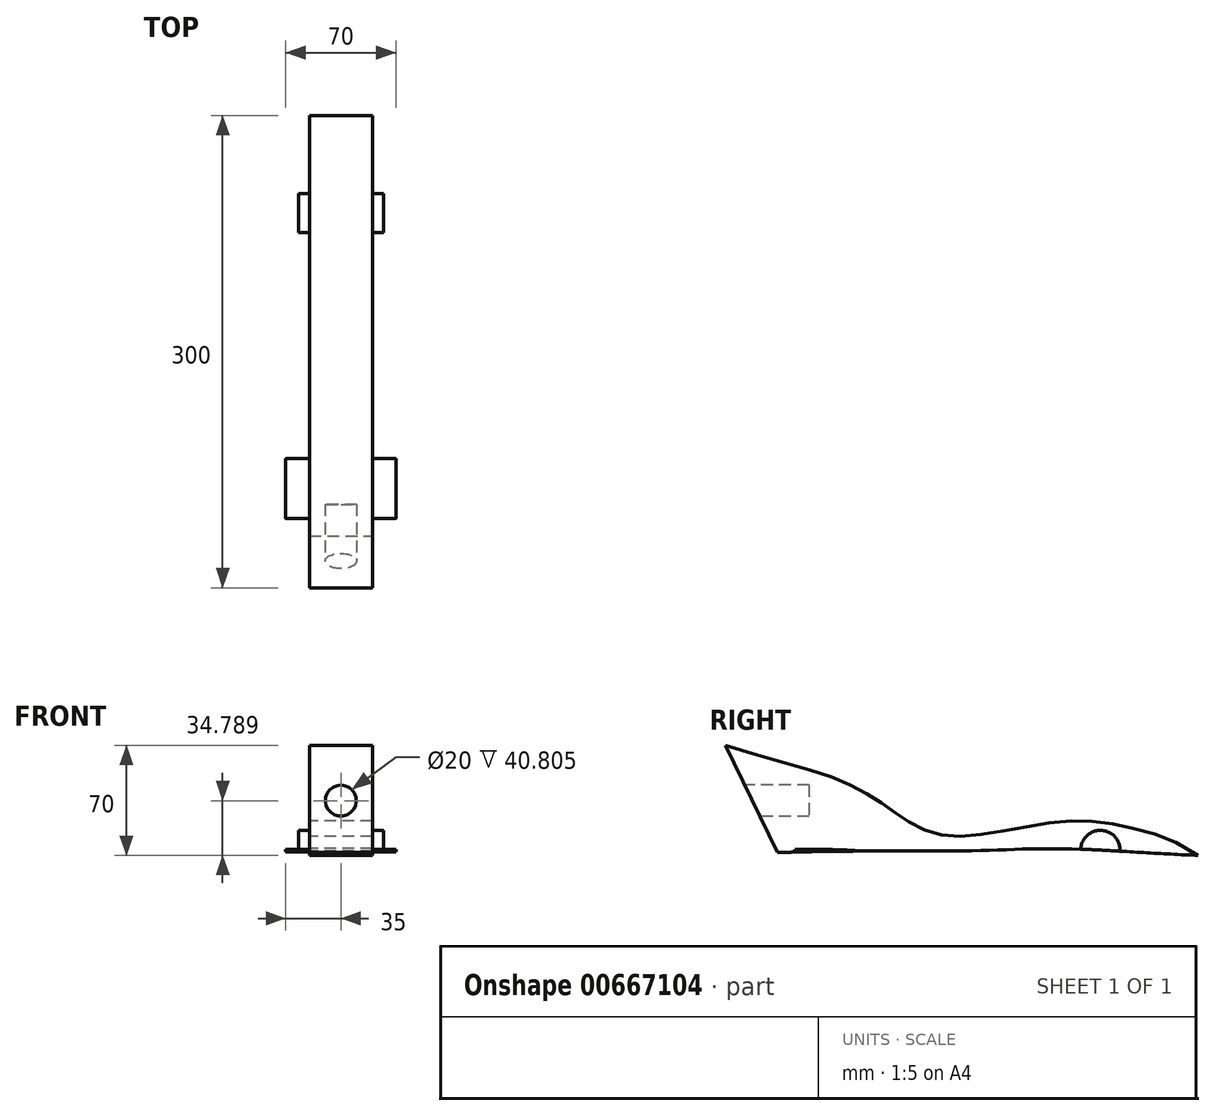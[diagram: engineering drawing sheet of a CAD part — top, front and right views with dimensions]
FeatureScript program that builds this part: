
annotation { "Feature Type Name" : "Feature", "Feature Type Description" : "" }
export const myFeature = defineFeature(function(context is Context, id is Id, definition is map)
    precondition{}
    {
        {
            var Q0;
            Q0=qCreatedBy(makeId("Top.planeOp"),FACE);
            var sketch = newSketch(context, id + "F0", { "sketchPlane" : qUnion([Q0])});
            skLineSegment(sketch, "E0.bottom", {"start": v(-20, 150) * mm, "end": v(20, 150) * mm});
            skLineSegment(sketch, "E0.top", {"start": v(-20, -150) * mm, "end": v(20, -150) * mm});
            skLineSegment(sketch, "E0.left", {"start": v(-20, 150) * mm, "end": v(-20, -150) * mm});
            skLineSegment(sketch, "E0.right", {"start": v(20, 150) * mm, "end": v(20, -150) * mm});
            skPoint(sketch, "E0.middle", {"position": v(0, 0) * mm});
            skSolve(sketch);
        }
        {
            var Q0;
            Q0=makeQuery(id+"F0.imprint","IMPRINT",FACE,{"disambiguationData":[TD([[makeQuery(id+"F0.imprint","IMPRINT",EDGE,{"derivedFrom":sQuery(id+"F0.wireOp",EDGE,"E0.bottom")}),-1.0]])]});
            extrude(context, id + "F1", {"entities" : qUnion([Q0]), "depth" : 70 * mm, "offsetDistance" : 25 * mm});
        }
        {
            var Q0;
            Q0=makeQuery(id+"F1.opExtrude","SWEPT_FACE",FACE,{"disambiguationData":[OSD([sQuery(id+"F0.wireOp",EDGE,"E0.right")])]});
            var sketch = newSketch(context, id + "F2", { "sketchPlane" : qUnion([Q0])});
            skLineSegment(sketch, "E1.0.0", {"start": v(-150, 0) * mm, "end": v(150, 0) * mm});
            skLineSegment(sketch, "E1.0.1", {"start": v(150, 0) * mm, "end": v(150, 70) * mm});
            skLineSegment(sketch, "E1.0.2", {"start": v(150, 70) * mm, "end": v(-150, 70) * mm});
            skLineSegment(sketch, "E1.0.3", {"start": v(-150, 70) * mm, "end": v(-150, 0) * mm});
            skFitSpline(sketch, "E2", {"points": [v(-150, 70) * mm, v(-85.62, 50.71) * mm, v(-56.21, 36.7) * mm, v(-35.87, 22.68) * mm, v(-12.23, 12.78) * mm, v(24.88, 15.26) * mm, v(69.68, 21.85) * mm, v(106.51, 17.73) * mm, v(150, 0) * mm], "startDerivative": vector(484.76, -154.9) * mm, "endDerivative": vector(326.98, -226.65) * mm});
            skFitSpline(sketch, "E3", {"points": [v(-150, 0) * mm, v(0, 2.89) * mm, v(63.63, 4.26) * mm, v(150, 0) * mm], "startDerivative": vector(390.02, 28.82) * mm, "endDerivative": vector(279.96, -11.51) * mm});
            skPoint(sketch, "E4.startSnap0", {"position": v(-150, 35) * mm});
            skLineSegment(sketch, "E5", {"start": v(-150, 70) * mm, "end": v(-116.13, 0) * mm});
            skSolve(sketch);
        }
        {
            var Q0;
            {var subQ0=sQuery(id+"F2.wireOp",EDGE,"E1.0.3");Q0=makeQuery(id+"F2.imprint","IMPRINT",FACE,{"disambiguationData":[TD([[makeQuery(id+"F2.imprint","IMPRINT",EDGE,{"derivedFrom":subQ0}),1.0]])]});}
            var Q1;
            {var subQ1=sQuery(id+"F2.wireOp",EDGE,"E1.0.0");var subQ3=sQuery(id+"F2.wireOp",EDGE,"E5");var subQ4=makeQuery(id+"F2.imprint","INTERSECT",VERTEX,{"derivedFrom":[subQ1,subQ3]});Q1=makeQuery(id+"F2.imprint","IMPRINT",FACE,{"disambiguationData":[TD([[makeQuery(id+"F2.imprint","IMPRINT",EDGE,{"disambiguationData":[TD([[subQ4,1.0]])],"derivedFrom":subQ3}),-1.0]])]});}
            var Q2;
            {var subQ1=sQuery(id+"F2.wireOp",EDGE,"E1.0.0");var subQ3=sQuery(id+"F2.wireOp",EDGE,"E5");var subQ4=makeQuery(id+"F2.imprint","INTERSECT",VERTEX,{"derivedFrom":[subQ1,subQ3]});Q2=makeQuery(id+"F2.imprint","IMPRINT",FACE,{"disambiguationData":[TD([[makeQuery(id+"F2.imprint","IMPRINT",EDGE,{"disambiguationData":[TD([[subQ4,1.0]])],"derivedFrom":subQ3}),1.0]])]});}
            var Q3;
            Q3=makeQuery(id+"F2.imprint","IMPRINT",FACE,{"disambiguationData":[TD([[makeQuery(id+"F2.imprint","IMPRINT",EDGE,{"derivedFrom":sQuery(id+"F2.wireOp",EDGE,"E1.0.1")}),-1.0]])]});
            var Q4;
            Q4=makeQuery(id+"F1.opExtrude","SWEPT_FACE",FACE,{"disambiguationData":[OSD([sQuery(id+"F0.wireOp",EDGE,"E0.left")])]});
            extrude(context, id + "F3", {"entities" : qUnion([Q0, Q1, Q2, Q3]), "operationType" : NewBodyOperationType.REMOVE, "endBound" : BoundingType.UP_TO_SURFACE, "oppositeDirection" : true, "depth" : 25 * mm, "endBoundEntityFace" : qUnion([Q4]), "offsetDistance" : 25 * mm});
        }
        {
            var Q0;
            Q0=qCreatedBy(makeId("Front.planeOp"),FACE);
            var Q1;
            {var subQ0=sQuery(id+"F2.wireOp",EDGE,"E5");var subQ1=sQuery(id+"F2.wireOp",EDGE,"E2");var subQ2=sQuery(id+"F2.wireOp",EDGE,"E1.0.3");var subQ3=sQuery(id+"F2.wireOp",EDGE,"E1.0.2");Q1=makeQuery(id+"F3.boolean.opBoolean","MERGE",EDGE,{"derivedFrom":[makeQuery(id+"F1.opExtrude","CAP_EDGE",EDGE,{"disambiguationData":[OSD([sQuery(id+"F0.wireOp",EDGE,"E0.top")])],"isStart":false}),makeQuery(id+"F3.opExtrude","SWEPT_EDGE",EDGE,{"disambiguationData":[OSD([subQ3,subQ2,subQ1,subQ0]),OD(0.0)]}),makeQuery(id+"F3.opExtrude","SWEPT_EDGE",EDGE,{"disambiguationData":[OSD([subQ3,subQ2,subQ1,subQ0]),OD(1.0)]})]});}
            cPlane(context, id + "F4", {"entities" : qUnion([Q0, Q1]), "cplaneType" : CPlaneType.LINE_ANGLE, "offset" : 147.7 * mm, "angle" : 0 * degree, "width" : 150 * mm, "height" : 150 * mm});
        }
        {
            var Q0;
            Q0=qCreatedBy(id+"F4.planeOp",FACE);
            var sketch = newSketch(context, id + "F5", { "sketchPlane" : qUnion([Q0])});
            skCircle(sketch, "E6", {"center": v(0, 34.79) * mm, "radius": 10 * mm});
            skSolve(sketch);
        }
        {
            var Q0;
            Q0=makeQuery(id+"F5.imprint","IMPRINT",FACE,{"disambiguationData":[TD([[makeQuery(id+"F5.imprint","IMPRINT",EDGE,{"derivedFrom":sQuery(id+"F5.wireOp",EDGE,"E6")}),1.0]])]});
            extrude(context, id + "F6", {"entities" : qUnion([Q0]), "operationType" : NewBodyOperationType.REMOVE, "depth" : 53 * mm, "offsetDistance" : 25 * mm});
        }
        {
            var Q0;
            Q0=makeQuery(id+"F1.opExtrude","SWEPT_FACE",FACE,{"disambiguationData":[OSD([sQuery(id+"F0.wireOp",EDGE,"E0.right")])]});
            var sketch = newSketch(context, id + "F7", { "sketchPlane" : qUnion([Q0])});
            skCircle(sketch, "E7", {"center": v(-87, 2.54) * mm, "radius": 19 * mm});
            skFitSpline(sketch, "E8.0.0", {"points": [v(150, 0) * mm, v(134.97, 10.42) * mm, v(107.36, 18.38) * mm, v(69.65, 24.4) * mm, v(25.52, 14.84) * mm, v(-12.02, 9.52) * mm, v(-36.37, 22) * mm, v(-56.2, 37.89) * mm, v(-87.67, 53.27) * mm, v(-123.35, 61.48) * mm, v(-150, 70) * mm]});
            skLineSegment(sketch, "E8.0.1", {"start": v(-150, 70) * mm, "end": v(-117, 1.79) * mm});
            skFitSpline(sketch, "E8.0.2", {"points": [v(-150, 0) * mm, v(-96.07, 3.99) * mm, v(-0.93, 1.22) * mm, v(61.68, 6.15) * mm, v(120.6, 1.2) * mm, v(150, 0) * mm]});
            skCircle(sketch, "E9", {"center": v(88, 3.39) * mm, "radius": 12.5 * mm});
            skSolve(sketch);
        }
        {
            var Q0;
            {var subQ0=sQuery(id+"F7.wireOp",EDGE,"ecc5208c-6ca3-4e4f-bc31-f04ef4dff16e.0");var subQ1=sQuery(id+"F7.wireOp",EDGE,"E7");var subQ2=makeQuery(id+"F7.imprint","INTERSECT",VERTEX,{"disambiguationData":[OD(0.0)],"derivedFrom":[subQ1,subQ0]});Q0=makeQuery(id+"F7.imprint","IMPRINT",FACE,{"disambiguationData":[TD([[makeQuery(id+"F7.imprint","IMPRINT",EDGE,{"disambiguationData":[TD([[subQ2,-1.0]])],"derivedFrom":subQ1}),1.0]])]});}
            var Q1;
            {var subQ0=sQuery(id+"F7.wireOp",EDGE,"E8.0.2");var subQ1=sQuery(id+"F7.wireOp",EDGE,"E7");var subQ2=makeQuery(id+"F7.imprint","INTERSECT",VERTEX,{"disambiguationData":[OD(0.0)],"derivedFrom":[subQ1,subQ0]});Q1=makeQuery(id+"F7.imprint","IMPRINT",FACE,{"disambiguationData":[TD([[makeQuery(id+"F7.imprint","IMPRINT",EDGE,{"disambiguationData":[TD([[subQ2,1.0]])],"derivedFrom":subQ1}),1.0]])]});}
            var Q2;
            {var subQ0=sQuery(id+"F7.wireOp",EDGE,"ecc5208c-6ca3-4e4f-bc31-f04ef4dff16e.0");var subQ1=sQuery(id+"F7.wireOp",EDGE,"E7");var subQ2=makeQuery(id+"F7.imprint","INTERSECT",VERTEX,{"disambiguationData":[OD(0.0)],"derivedFrom":[subQ1,subQ0]});Q2=makeQuery(id+"F7.imprint","IMPRINT",FACE,{"disambiguationData":[TD([[makeQuery(id+"F7.imprint","IMPRINT",EDGE,{"disambiguationData":[TD([[subQ2,1.0]])],"derivedFrom":subQ1}),1.0]])]});}
            extrude(context, id + "F8", {"entities" : qUnion([Q0, Q1, Q2]), "depth" : 15 * mm, "offsetDistance" : 25 * mm});
        }
        {
            var Q0;
            Q0=makeQuery(id+"F8.opExtrude","SWEPT_BODY",BODY,{"disambiguationData":[OSD([sQuery(id+"F7.wireOp",EDGE,"E7")])]});
            var Q1;
            Q1=makeQuery(id+"F8.opExtrude","SWEPT_BODY",BODY,{"disambiguationData":[OSD([sQuery(id+"F7.wireOp",EDGE,"E9")])]});
            var Q2;
            Q2=qCreatedBy(makeId("Right.planeOp"),FACE);
            mirror(context, id + "F9", {"entities" : qUnion([Q0, Q1]), "mirrorPlane" : qUnion([Q2])});
        }
        {
            var Q0;
            {var subQ0=sQuery(id+"F7.wireOp",EDGE,"E9");var subQ1=sQuery(id+"F7.wireOp",EDGE,"E8.0.2");var subQ2=makeQuery(id+"F7.imprint","INTERSECT",VERTEX,{"disambiguationData":[OD(0.0)],"derivedFrom":[subQ1,subQ0]});Q0=makeQuery(id+"F7.imprint","IMPRINT",FACE,{"disambiguationData":[TD([[makeQuery(id+"F7.imprint","IMPRINT",EDGE,{"disambiguationData":[TD([[subQ2,-1.0]])],"derivedFrom":subQ1}),-1.0]])]});}
            var Q1;
            {var subQ0=sQuery(id+"F7.wireOp",EDGE,"E9");var subQ1=sQuery(id+"F7.wireOp",EDGE,"E8.0.2");var subQ2=makeQuery(id+"F7.imprint","INTERSECT",VERTEX,{"disambiguationData":[OD(0.0)],"derivedFrom":[subQ1,subQ0]});Q1=makeQuery(id+"F7.imprint","IMPRINT",FACE,{"disambiguationData":[TD([[makeQuery(id+"F7.imprint","IMPRINT",EDGE,{"disambiguationData":[TD([[subQ2,-1.0]])],"derivedFrom":subQ1}),1.0]])]});}
            extrude(context, id + "F10", {"entities" : qUnion([Q0, Q1]), "depth" : 7 * mm, "offsetDistance" : 25 * mm});
        }
        {
            var Q0;
            Q0=makeQuery(id+"F10.opExtrude","SWEPT_BODY",BODY,{"disambiguationData":[OSD([sQuery(id+"F7.wireOp",EDGE,"E9")])]});
            var Q1;
            Q1=qCreatedBy(makeId("Right.planeOp"),FACE);
            mirror(context, id + "F11", {"entities" : qUnion([Q0]), "mirrorPlane" : qUnion([Q1])});
        }
    });
